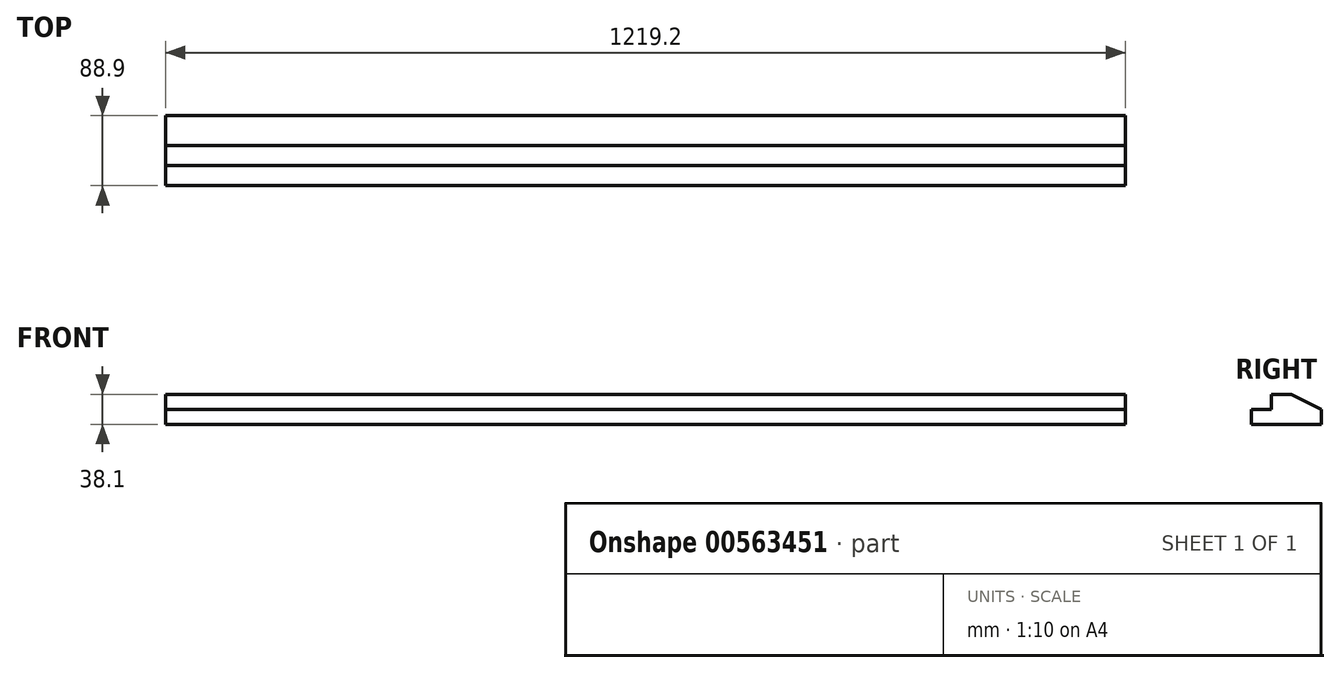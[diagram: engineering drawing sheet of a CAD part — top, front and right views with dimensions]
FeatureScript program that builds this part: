
annotation { "Feature Type Name" : "Feature", "Feature Type Description" : "" }
export const myFeature = defineFeature(function(context is Context, id is Id, definition is map)
    precondition{}
    {
        {
            var Q0;
            Q0=qCreatedBy(makeId("Top.planeOp"),FACE);
            var sketch = newSketch(context, id + "F0", { "sketchPlane" : qUnion([Q0])});
            skLineSegment(sketch, "E0.bottom", {"start": v(-256.04, 47) * mm, "end": v(963.16, 47) * mm});
            skLineSegment(sketch, "E0.top", {"start": v(-256.04, -41.9) * mm, "end": v(963.16, -41.9) * mm});
            skLineSegment(sketch, "E0.left", {"start": v(-256.04, 47) * mm, "end": v(-256.04, -41.9) * mm});
            skLineSegment(sketch, "E0.right", {"start": v(963.16, 47) * mm, "end": v(963.16, -41.9) * mm});
            skLineSegment(sketch, "E1", {"start": v(-256.04, -16.5) * mm, "end": v(963.16, -16.5) * mm});
            skSolve(sketch);
        }
        {
            var Q0;
            {var subQ0=sQuery(id+"F0.wireOp",EDGE,"E0.bottom");Q0=makeQuery(id+"F0.imprint","IMPRINT",FACE,{"disambiguationData":[TD([[makeQuery(id+"F0.imprint","IMPRINT",EDGE,{"derivedFrom":subQ0}),-1.0]])]});}
            extrude(context, id + "F1", {"entities" : qUnion([Q0]), "depth" : 19.05 * mm, "offsetDistance" : 25.4 * mm});
        }
        {
            var Q0;
            Q0 = qSketchRegion(id + "F0", true);
            extrude(context, id + "F2", {"entities" : qUnion([Q0]), "operationType" : NewBodyOperationType.ADD, "depth" : -19.05 * mm, "offsetDistance" : 25.4 * mm});
        }
        {
            var Q0;
            Q0=makeQuery(id+"F1.opExtrude","CAP_EDGE",EDGE,{"disambiguationData":[OSD([sQuery(id+"F0.wireOp",EDGE,"E0.bottom")])],"isStart":false});
            chamfer(context, id + "F3", {"entities" : qUnion([Q0]), "chamferType" : ChamferType.TWO_OFFSETS, "width1" : 19.05 * mm, "oppositeDirection" : false, "width2" : 38.1 * mm, "tangentPropagation" : true});
        }
    });
